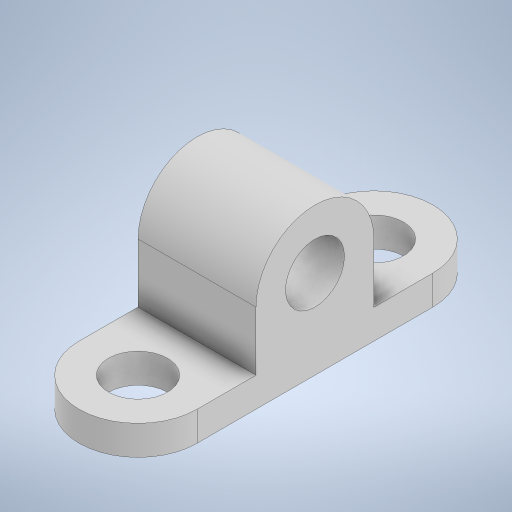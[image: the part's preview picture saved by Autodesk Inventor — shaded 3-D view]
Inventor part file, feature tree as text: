
AUTODESK INVENTOR PART (.ipt)
format: ipt  version: 2024 (Build 280153000, 153)  size: 252,928 bytes
history: native  units: mm
features: extrude x2, sketch x2
ambient origin geometry x8: Origin, YZ Plane, XZ Plane, XY Plane, X Axis, Y Axis, Z Axis, Center Point
bodies: Solid1 (feature_tree)
feature tree (4):
  extrude  "Extrusion1"  Depth=40.0mm
  extrude  "Extrusion2"  Depth=40.0mm
  sketch  "Sketch1"  dims[d0=40.0mm d1=40.0mm]
  sketch  "Sketch2"  dims[d3=20.0mm d4=40.0mm d6=20.0mm d7=40.0mm d8=10.0mm d9=0.0mm d11=40.0mm d12=20.0mm d13=40.0mm d14=0.0mm]
